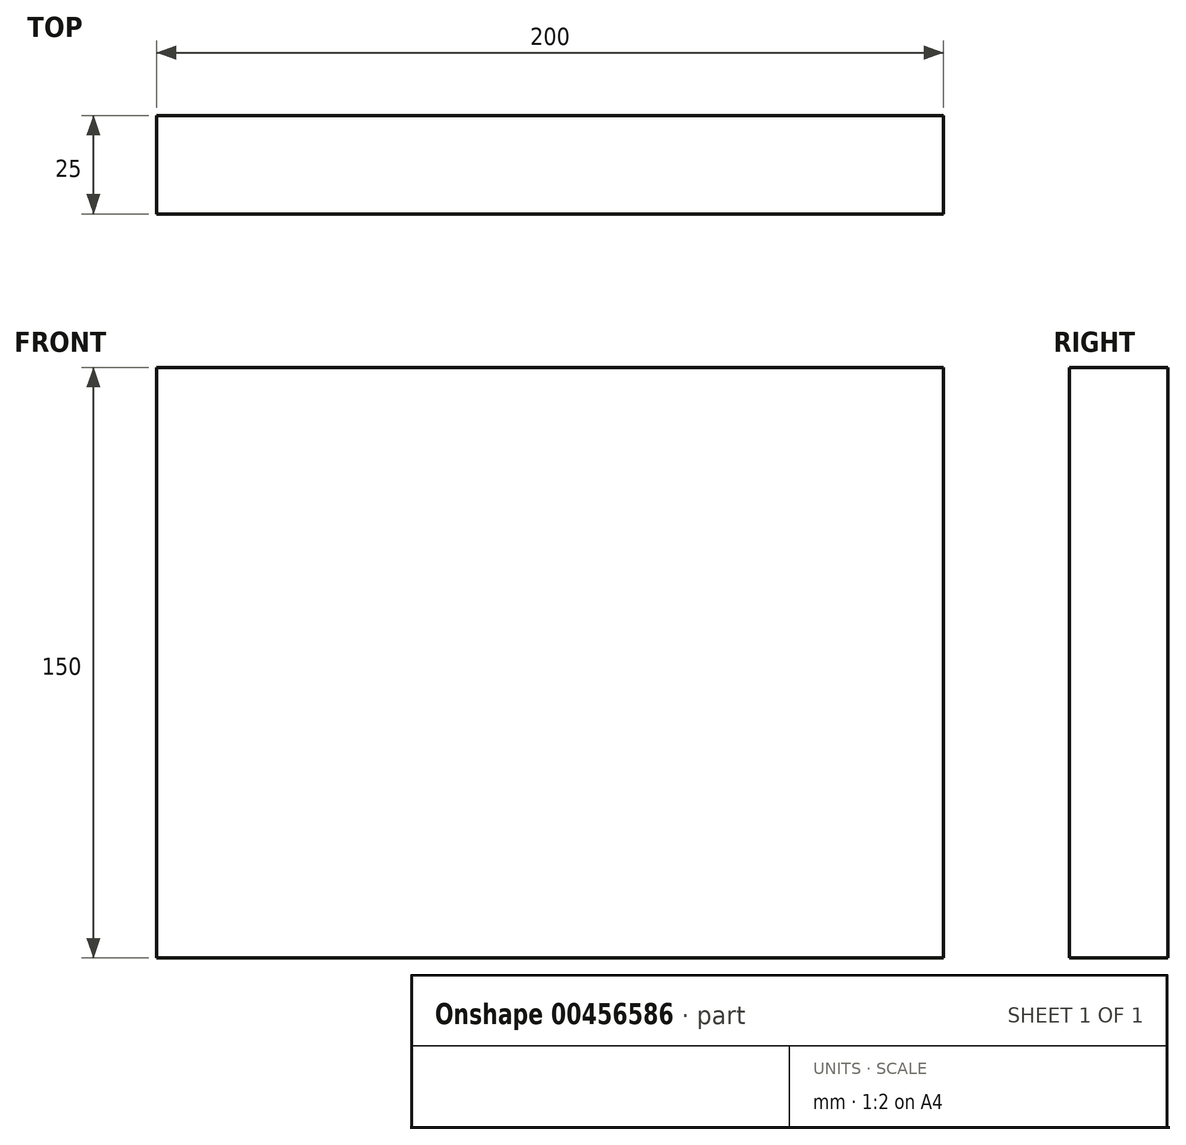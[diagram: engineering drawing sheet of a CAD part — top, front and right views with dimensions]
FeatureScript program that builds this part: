
annotation { "Feature Type Name" : "Feature", "Feature Type Description" : "" }
export const myFeature = defineFeature(function(context is Context, id is Id, definition is map)
    precondition{}
    {
        {
            var Q0;
            Q0=qCreatedBy(makeId("Front.planeOp"),FACE);
            var sketch = newSketch(context, id + "F0", { "sketchPlane" : qUnion([Q0])});
            skLineSegment(sketch, "E0.bottom", {"start": v(-101.63, 107.3) * mm, "end": v(98.37, 107.3) * mm});
            skLineSegment(sketch, "E0.top", {"start": v(-101.63, -42.7) * mm, "end": v(98.37, -42.7) * mm});
            skLineSegment(sketch, "E0.left", {"start": v(-101.63, 107.3) * mm, "end": v(-101.63, -42.7) * mm});
            skLineSegment(sketch, "E0.right", {"start": v(98.37, 107.3) * mm, "end": v(98.37, -42.7) * mm});
            skSolve(sketch);
        }
        {
            var Q0;
            Q0=qSketchRegion(id+"F0",true);
            extrude(context, id + "F1", {"entities" : qUnion([Q0]), "depth" : 25 * mm});
        }
    });
